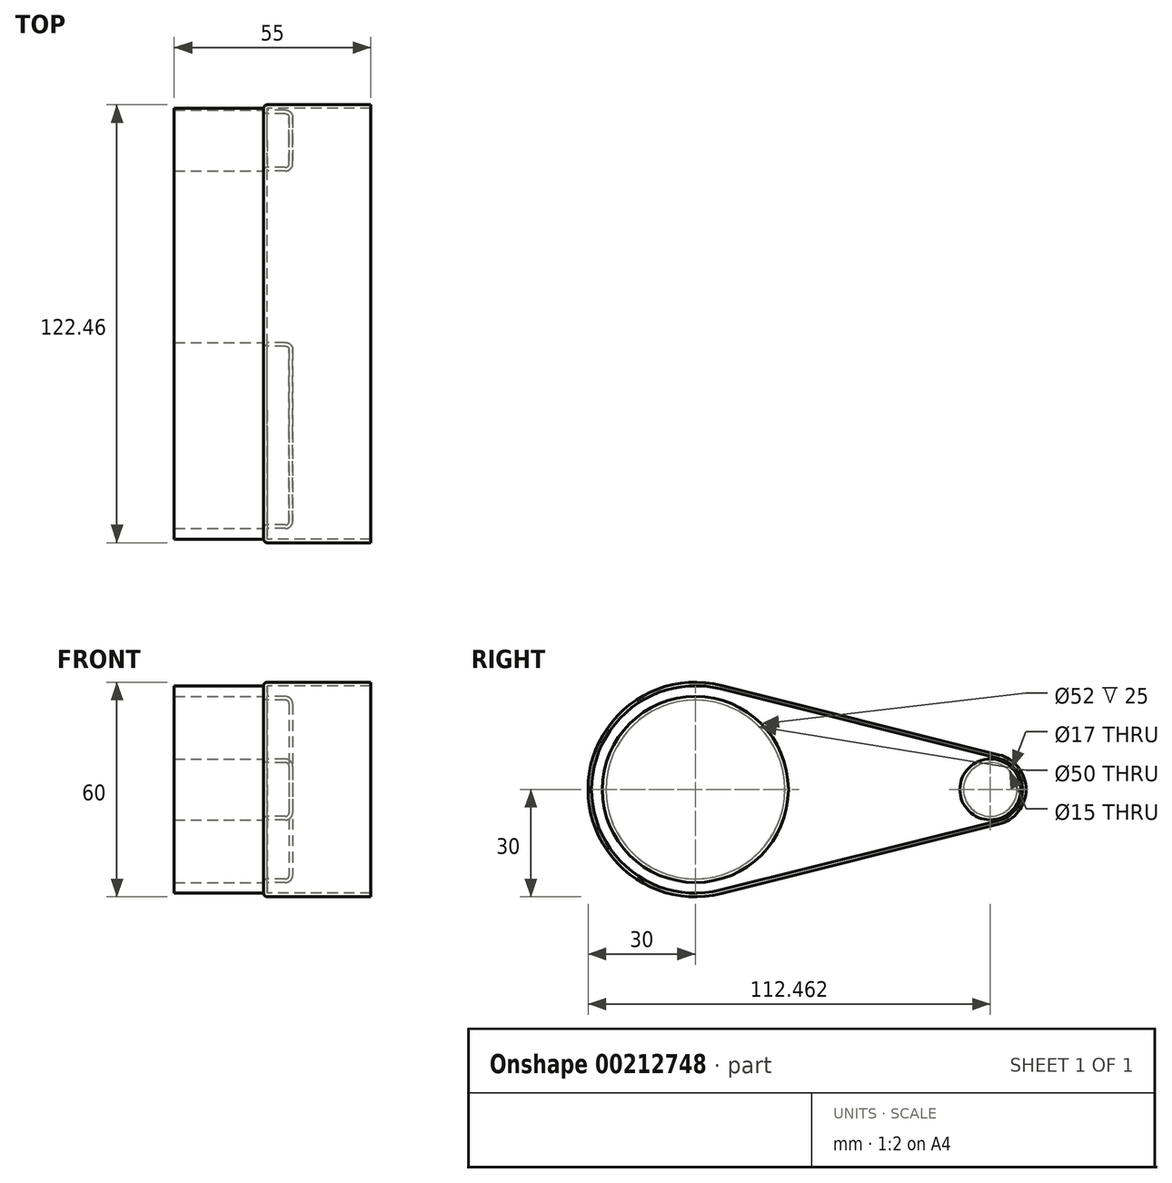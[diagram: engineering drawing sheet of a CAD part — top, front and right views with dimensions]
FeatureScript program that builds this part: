
annotation { "Feature Type Name" : "Feature", "Feature Type Description" : "" }
export const myFeature = defineFeature(function(context is Context, id is Id, definition is map)
    precondition{}
    {
        {
            var Q0;
            Q0=qCreatedBy(makeId("Right.planeOp"),FACE);
            var sketch = newSketch(context, id + "F0", { "sketchPlane" : qUnion([Q0])});
            skCircle(sketch, "E0", {"center": v(0, 0) * mm, "radius": 30 * mm});
            skCircle(sketch, "E1", {"center": v(82.46, 0) * mm, "radius": 10 * mm});
            skLineSegment(sketch, "E2", {"start": v(7.28, 29.1) * mm, "end": v(84.89, 9.7) * mm});
            skLineSegment(sketch, "E3", {"start": v(7.28, -29.1) * mm, "end": v(84.89, -9.7) * mm});
            skSolve(sketch);
        }
        {
            var Q0;
            {var subQ0=sQuery(id+"F0.wireOp",EDGE,"E0");var subQ1=makeQuery(id+"F0.imprint","INTERSECT",VERTEX,{"derivedFrom":[subQ0,sQuery(id+"F0.wireOp",EDGE,"E2")]});Q0=makeQuery(id+"F0.imprint","IMPRINT",FACE,{"disambiguationData":[TD([[makeQuery(id+"F0.imprint","IMPRINT",EDGE,{"disambiguationData":[TD([[subQ1,-1.0]])],"derivedFrom":subQ0}),1.0]])]});}
            var Q1;
            {var subQ0=sQuery(id+"F0.wireOp",EDGE,"E2");Q1=makeQuery(id+"F0.imprint","IMPRINT",FACE,{"disambiguationData":[TD([[makeQuery(id+"F0.imprint","IMPRINT",EDGE,{"derivedFrom":subQ0}),-1.0]])]});}
            var Q2;
            {var subQ0=sQuery(id+"F0.wireOp",EDGE,"E1");var subQ1=makeQuery(id+"F0.imprint","INTERSECT",VERTEX,{"derivedFrom":[subQ0,sQuery(id+"F0.wireOp",EDGE,"E2")]});Q2=makeQuery(id+"F0.imprint","IMPRINT",FACE,{"disambiguationData":[TD([[makeQuery(id+"F0.imprint","IMPRINT",EDGE,{"disambiguationData":[TD([[subQ1,-1.0]])],"derivedFrom":subQ0}),1.0]])]});}
            extrude(context, id + "F1", {"entities" : qUnion([Q0, Q1, Q2]), "depth" : 30 * mm});
        }
        {
            var Q0;
            Q0=makeQuery(id+"F1.opExtrude","CAP_FACE",FACE,{"disambiguationData":[OSD([sQuery(id+"F0.wireOp",EDGE,"E0"),sQuery(id+"F0.wireOp",EDGE,"E1"),sQuery(id+"F0.wireOp",EDGE,"E2"),sQuery(id+"F0.wireOp",EDGE,"E3")])],"isStart":true});
            var sketch = newSketch(context, id + "F2", { "sketchPlane" : qUnion([Q0])});
            skCircle(sketch, "E4", {"center": v(0, 0) * mm, "radius": 25 * mm});
            skCircle(sketch, "E5", {"center": v(-82.46, 0) * mm, "radius": 7.5 * mm});
            skSolve(sketch);
        }
        {
            var Q0;
            Q0=makeQuery(id+"F2.imprint","IMPRINT",FACE,{"disambiguationData":[TD([[makeQuery(id+"F2.imprint","IMPRINT",EDGE,{"derivedFrom":sQuery(id+"F2.wireOp",EDGE,"E4")}),1.0]])]});
            var Q1;
            Q1=makeQuery(id+"F2.imprint","IMPRINT",FACE,{"disambiguationData":[TD([[makeQuery(id+"F2.imprint","IMPRINT",EDGE,{"derivedFrom":sQuery(id+"F2.wireOp",EDGE,"E5")}),1.0]])]});
            var Q2;
            Q2=sQuery(id+"F2.wireOp",EDGE,"E4");
            var Q3;
            Q3=sQuery(id+"F2.wireOp",EDGE,"E5");
            extrude(context, id + "F3", {"entities" : qUnion([Q0, Q1]), "operationType" : NewBodyOperationType.REMOVE, "surfaceEntities" : qUnion([Q2, Q3]), "oppositeDirection" : true, "depth" : 7.1 * mm});
        }
        {
            var Q0;
            Q0=makeQuery(id+"F1.opExtrude","CAP_FACE",FACE,{"disambiguationData":[OSD([sQuery(id+"F0.wireOp",EDGE,"E0"),sQuery(id+"F0.wireOp",EDGE,"E1"),sQuery(id+"F0.wireOp",EDGE,"E2"),sQuery(id+"F0.wireOp",EDGE,"E3")])],"isStart":true});
            var Q1;
            Q1=makeQuery(id+"F3.boolean.opBoolean","COPY",FACE,{"derivedFrom":makeQuery(id+"F3.opExtrude","CAP_FACE",FACE,{"disambiguationData":[OSD([sQuery(id+"F2.wireOp",EDGE,"E4")])],"isStart":false})});
            var Q2;
            Q2=makeQuery(id+"F3.boolean.opBoolean","COPY",FACE,{"derivedFrom":makeQuery(id+"F3.opExtrude","CAP_FACE",FACE,{"disambiguationData":[OSD([sQuery(id+"F2.wireOp",EDGE,"E5")])],"isStart":false})});
            fillet(context, id + "F4", {"entities" : qUnion([Q0, Q1, Q2]), "radius" : 1 * mm, "tangentPropagation" : true, "allowEdgeOverflow" : false});
        }
        {
            var Q0;
            Q0=makeQuery(id+"F1.opExtrude","CAP_FACE",FACE,{"disambiguationData":[OSD([sQuery(id+"F0.wireOp",EDGE,"E0"),sQuery(id+"F0.wireOp",EDGE,"E1"),sQuery(id+"F0.wireOp",EDGE,"E2"),sQuery(id+"F0.wireOp",EDGE,"E3")])],"isStart":false});
            shell(context, id + "F5", {"entities" : qUnion([Q0]), "thickness" : 1 * mm});
        }
        {
            var Q0;
            Q0=makeQuery(id+"F1.opExtrude","CAP_FACE",FACE,{"disambiguationData":[OSD([sQuery(id+"F0.wireOp",EDGE,"E0"),sQuery(id+"F0.wireOp",EDGE,"E1"),sQuery(id+"F0.wireOp",EDGE,"E2"),sQuery(id+"F0.wireOp",EDGE,"E3")])],"isStart":true});
            var sketch = newSketch(context, id + "F7", { "sketchPlane" : qUnion([Q0])});
            skSolve(sketch);
        }
        {
            var Q0;
            {var subQ0=sQuery(id+"F0.wireOp",EDGE,"E3");var subQ1=sQuery(id+"F0.wireOp",EDGE,"E2");var subQ2=sQuery(id+"F0.wireOp",EDGE,"E1");var subQ3=sQuery(id+"F0.wireOp",EDGE,"E0");var subQ4=makeQuery(id+"F1.opExtrude","CAP_FACE",FACE,{"disambiguationData":[OSD([subQ3,subQ2,subQ1,subQ0])],"isStart":true});Q0=makeQuery(id+"F7.imprint","IMPRINT",FACE,{"disambiguationData":[TD([[makeQuery(id+"F7.imprint","IMPRINT",EDGE,{"derivedFrom":makeQuery(id+"F4.opFillet","BLEND_EDGE",EDGE,{"blendedFrom":[makeQuery(id+"F1.opExtrude","CAP_EDGE",EDGE,{"disambiguationData":[OSD([subQ3])],"isStart":true}),subQ4],"blendedInto":[subQ4]})}),1.0]])]});}
            extrude(context, id + "F6", {"entities" : qUnion([Q0]), "operationType" : NewBodyOperationType.ADD, "depth" : 25 * mm});
        }
    });
